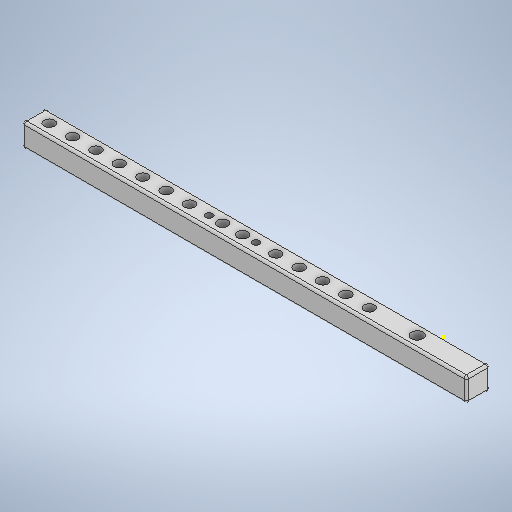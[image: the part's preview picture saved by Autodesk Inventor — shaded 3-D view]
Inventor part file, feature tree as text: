
AUTODESK INVENTOR PART (.ipt)
format: ipt  version: 2025.2 (Build 292293000, 293)  size: 355,328 bytes
history: native  units: in
note: dims shown in document units (in); Inventor stores cm internally (conversion verified against a paired STEP export)
features: sketch x11, extrude x9, thread x2, fillet x2
ambient origin geometry x8: Origin, YZ Plane, XZ Plane, XY Plane, X Axis, Y Axis, Z Axis, Center Point
bodies: Solid1 (feature_tree)
feature tree (24):
  extrude  "Extrusion1"  Depth=0.3937in
  sketch  "Sketch2"  dims[d8=0.1181in d9=0.1181in]
  extrude  "Extrusion2"  Depth=0.3937in
  extrude  "Extrusion3"  Depth=0.1181in
  extrude  "Extrusion4"  Depth=0.3937in TaperAngle=0.0deg
  extrude  "Extrusion5"  Depth=0.3937in
  thread  "Thread1"  [1 undecoded]
  thread  "Thread2"  [1 undecoded]
  extrude  "Extrusion6"  Depth=0.3937in TaperAngle=0.0deg
  extrude  "Extrusion7"  Depth=0.3937in TaperAngle=0.0deg
  extrude  "Extrusion8"  Depth=0.0394in
  sketch  "Sketch7"  dims[d54=0.3937in d55=0.0in]
  fillet  "Fillet3"  Radius=0.0394in
  fillet  "Fillet4"  Radius=0.1969in
  sketch  "Sketch8"
  extrude  "Extrusion9"  [1 undecoded]
  sketch  "Sketch1"  dims[d0=6.6929in d1=0.3937in]
  sketch  "Sketch3"  dims[d14=0.3937in d15=0.0in d18=2.7559in d20=0.3937in d21=0.3937in d23=0.3937in d30=2.3622in d32=0.3937in d33=0.3937in d35=0.3937in d37=0.3937in d38=0.0in]
  sketch  "Sketch Rectangular Pattern1"  dims[d2=0.3937in d3=0.0in d4=0.0866in]
  sketch  "Sketch Rectangular Pattern2"  dims[d10=0.3937in d11=0.0in d12=0.3937in d13=0.0in]
  sketch  "Sketch4"  dims[d39=0.3937in d40=0.0in d41=0.3937in d42=0.0in]
  sketch  "Sketch5"  dims[d44=0.3937in d45=0.0in d46=0.3937in d47=0.0in]
  sketch  "Sketch6"  dims[d49=0.3937in d50=0.0in d51=0.0394in d52=0.0394in d53=0.1969in]
  sketch  "Sketch9"
note: 3 required parameter values undecoded (feature->parameter linkage not recoverable at this tier; creation-order binding heuristic only, values carry confidence <= 0.55)
